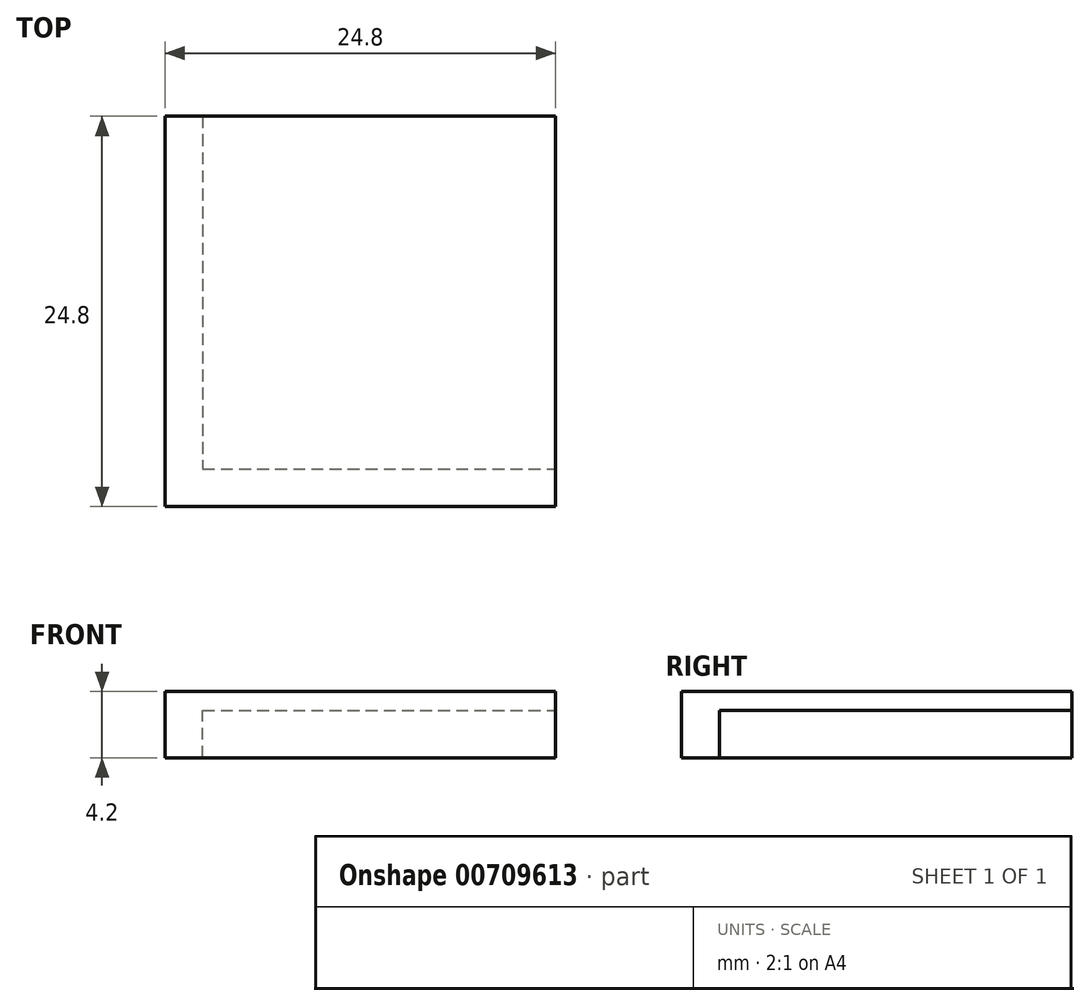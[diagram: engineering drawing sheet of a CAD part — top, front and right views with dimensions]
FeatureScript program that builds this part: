
annotation { "Feature Type Name" : "Feature", "Feature Type Description" : "" }
export const myFeature = defineFeature(function(context is Context, id is Id, definition is map)
    precondition{}
    {
        {
            var Q0;
            Q0=qCreatedBy(makeId("Top.planeOp"),FACE);
            var sketch = newSketch(context, id + "F0", { "sketchPlane" : qUnion([Q0])});
            skPoint(sketch, "E0.middle", {"position": v(0, 0) * mm});
            skLineSegment(sketch, "E1.bottom", {"start": v(-12.4, 12.4) * mm, "end": v(12.4, 12.4) * mm});
            skLineSegment(sketch, "E1.top", {"start": v(-12.4, -12.4) * mm, "end": v(12.4, -12.4) * mm});
            skLineSegment(sketch, "E1.left", {"start": v(-12.4, 12.4) * mm, "end": v(-12.4, -12.4) * mm});
            skLineSegment(sketch, "E1.right", {"start": v(12.4, 12.4) * mm, "end": v(12.4, -12.4) * mm});
            skPoint(sketch, "E0.left.start.orphan", {"position": v(5, 5) * mm});
            skLineSegment(sketch, "E2.top", {"start": v(-10, -10) * mm, "end": v(10, -10) * mm});
            skLineSegment(sketch, "E2.left", {"start": v(-10, 10) * mm, "end": v(-10, -10) * mm});
            skLineSegment(sketch, "E3", {"start": v(-10, 10) * mm, "end": v(-10, 12.4) * mm});
            skLineSegment(sketch, "E4", {"start": v(10, -10) * mm, "end": v(12.4, -10) * mm});
            skSolve(sketch);
        }
        {
            var Q0;
            {var subQ1=sQuery(id+"F0.wireOp",EDGE,"E1.top");Q0=makeQuery(id+"F0.imprint","IMPRINT",FACE,{"disambiguationData":[TD([[makeQuery(id+"F0.imprint","IMPRINT",EDGE,{"derivedFrom":subQ1}),1.0]])]});}
            var Q1;
            Q1=makeQuery(id+"F0.imprint","IMPRINT",FACE,{"disambiguationData":[TD([[makeQuery(id+"F0.imprint","IMPRINT",EDGE,{"derivedFrom":sQuery(id+"F0.wireOp",EDGE,"E2.top")}),1.0]])]});
            extrude(context, id + "F1", {"entities" : qUnion([Q0, Q1]), "depth" : 1.2 * mm, "offsetDistance" : 25 * mm});
        }
        {
            var Q0;
            {var subQ1=sQuery(id+"F0.wireOp",EDGE,"E1.top");Q0=makeQuery(id+"F0.imprint","IMPRINT",FACE,{"disambiguationData":[TD([[makeQuery(id+"F0.imprint","IMPRINT",EDGE,{"derivedFrom":subQ1}),1.0]])]});}
            extrude(context, id + "F2", {"entities" : qUnion([Q0]), "operationType" : NewBodyOperationType.ADD, "oppositeDirection" : true, "depth" : 3 * mm, "offsetDistance" : 25 * mm});
        }
    });
